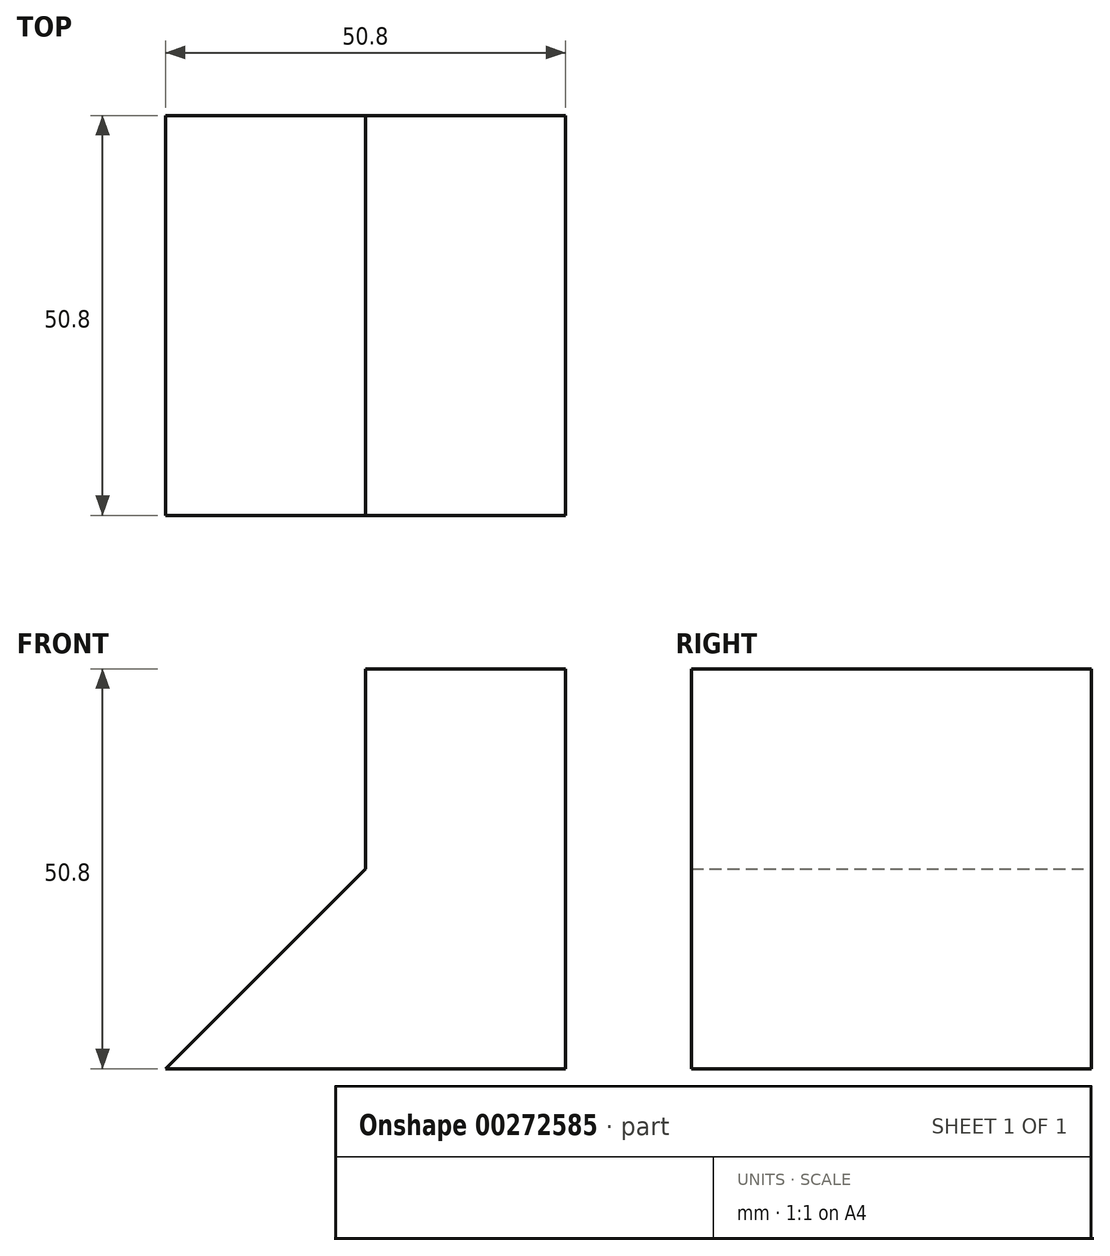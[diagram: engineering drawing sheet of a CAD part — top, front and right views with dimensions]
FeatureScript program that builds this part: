
annotation { "Feature Type Name" : "Feature", "Feature Type Description" : "" }
export const myFeature = defineFeature(function(context is Context, id is Id, definition is map)
    precondition{}
    {
        {
            var Q0;
            Q0=qCreatedBy(makeId("Front.planeOp"),FACE);
            var sketch = newSketch(context, id + "F0", { "sketchPlane" : qUnion([Q0])});
            skLineSegment(sketch, "E0", {"start": v(-49.84, 49.08) * mm, "end": v(-24.44, 49.08) * mm});
            skLineSegment(sketch, "E1", {"start": v(-24.44, 49.08) * mm, "end": v(-24.44, -1.72) * mm});
            skLineSegment(sketch, "E2", {"start": v(-24.44, -1.72) * mm, "end": v(-75.24, -1.72) * mm});
            skLineSegment(sketch, "E3", {"start": v(-49.84, 49.08) * mm, "end": v(-49.84, 23.68) * mm});
            skLineSegment(sketch, "E4", {"start": v(-49.84, 23.68) * mm, "end": v(-75.24, -1.72) * mm});
            skSolve(sketch);
        }
        {
            var Q0;
            Q0=makeQuery(id+"F0.imprint","IMPRINT",FACE,{"disambiguationData":[TD([[makeQuery(id+"F0.imprint","IMPRINT",EDGE,{"derivedFrom":sQuery(id+"F0.wireOp",EDGE,"E0")}),-1.0]])]});
            extrude(context, id + "F1", {"entities" : qUnion([Q0]), "depth" : 50.8 * mm});
        }
    });
